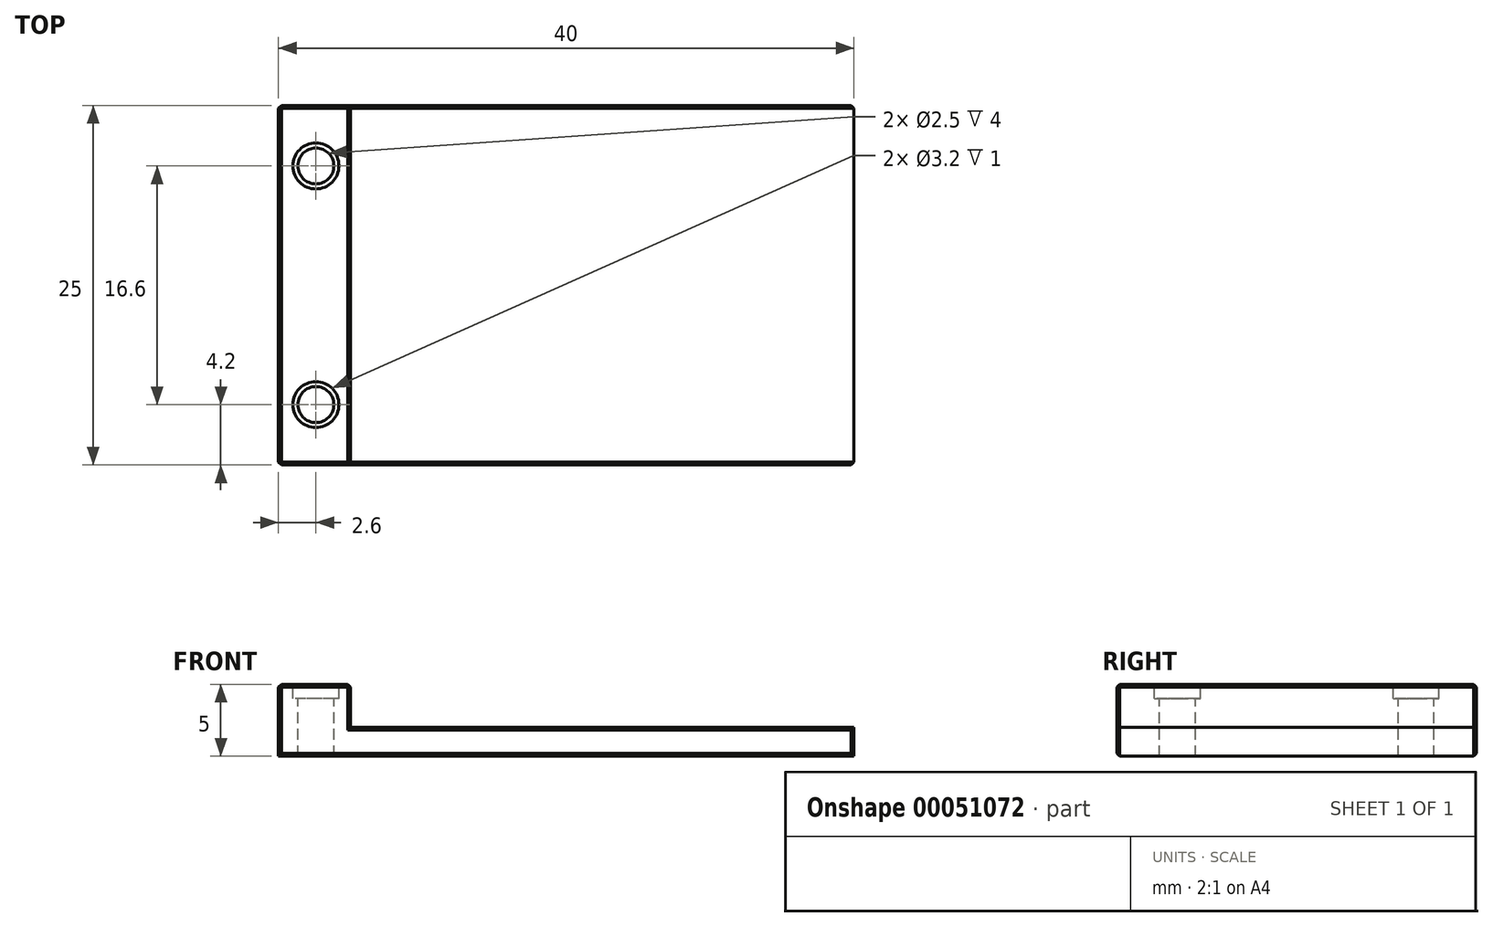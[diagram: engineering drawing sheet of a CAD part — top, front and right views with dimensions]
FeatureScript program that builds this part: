
annotation { "Feature Type Name" : "Feature", "Feature Type Description" : "" }
export const myFeature = defineFeature(function(context is Context, id is Id, definition is map)
    precondition{}
    {
        {
            var Q0;
            Q0=qCreatedBy(makeId("Top.planeOp"),FACE);
            var sketch = newSketch(context, id + "F0", { "sketchPlane" : qUnion([Q0])});
            skLineSegment(sketch, "E0.bottom", {"start": v(0, 0) * mm, "end": v(40, 0) * mm});
            skLineSegment(sketch, "E0.top", {"start": v(0, 25) * mm, "end": v(40, 25) * mm});
            skLineSegment(sketch, "E0.left", {"start": v(0, 0) * mm, "end": v(0, 25) * mm});
            skLineSegment(sketch, "E0.right", {"start": v(40, 0) * mm, "end": v(40, 25) * mm});
            skSolve(sketch);
        }
        {
            var Q0;
            Q0=makeQuery(id+"F0.imprint","IMPRINT",FACE,{"disambiguationData":[TD([[makeQuery(id+"F0.imprint","IMPRINT",EDGE,{"derivedFrom":sQuery(id+"F0.wireOp",EDGE,"E0.bottom")}),1.0]])]});
            extrude(context, id + "F1", {"entities" : qUnion([Q0]), "depth" : 5 * mm});
        }
        {
            var Q0;
            Q0=makeQuery(id+"F1.opExtrude","SWEPT_FACE",FACE,{"disambiguationData":[OSD([sQuery(id+"F0.wireOp",EDGE,"E0.bottom")])]});
            var sketch = newSketch(context, id + "F2", { "sketchPlane" : qUnion([Q0])});
            skLineSegment(sketch, "E1.bottom", {"start": v(5, 5) * mm, "end": v(40, 5) * mm});
            skLineSegment(sketch, "E1.top", {"start": v(5, 2) * mm, "end": v(40, 2) * mm});
            skLineSegment(sketch, "E1.left", {"start": v(5, 5) * mm, "end": v(5, 2) * mm});
            skLineSegment(sketch, "E1.right", {"start": v(40, 5) * mm, "end": v(40, 2) * mm});
            skSolve(sketch);
        }
        {
            var Q0;
            Q0 = qSketchRegion(id + "F2", true);
            extrude(context, id + "F3", {"entities" : qUnion([Q0]), "operationType" : NewBodyOperationType.REMOVE, "oppositeDirection" : true, "depth" : 25 * mm});
        }
        {
            var Q0;
            Q0=makeQuery(id+"F1.opExtrude","CAP_FACE",FACE,{"disambiguationData":[OSD([sQuery(id+"F0.wireOp",EDGE,"E0.bottom"),sQuery(id+"F0.wireOp",EDGE,"E0.top"),sQuery(id+"F0.wireOp",EDGE,"E0.left"),sQuery(id+"F0.wireOp",EDGE,"E0.right")])],"isStart":false});
            var Q1;
            Q1=makeQuery(id+"F1.opExtrude","SWEPT_FACE",FACE,{"disambiguationData":[OSD([sQuery(id+"F0.wireOp",EDGE,"E0.bottom")])]});
            var Q2;
            Q2=makeQuery(id+"F1.opExtrude","SWEPT_FACE",FACE,{"disambiguationData":[OSD([sQuery(id+"F0.wireOp",EDGE,"E0.top")])]});
            chamfer(context, id + "F4", {"entities" : qUnion([Q0, Q1, Q2]), "width" : 0.2 * mm, "tangentPropagation" : true});
        }
        {
            var Q0;
            Q0=makeQuery(id+"F1.opExtrude","CAP_FACE",FACE,{"disambiguationData":[OSD([sQuery(id+"F0.wireOp",EDGE,"E0.bottom"),sQuery(id+"F0.wireOp",EDGE,"E0.top"),sQuery(id+"F0.wireOp",EDGE,"E0.left"),sQuery(id+"F0.wireOp",EDGE,"E0.right")])],"isStart":false});
            var sketch = newSketch(context, id + "F5", { "sketchPlane" : qUnion([Q0])});
            skCircle(sketch, "E2", {"center": v(2.6, 20.8) * mm, "radius": 1.25 * mm});
            skSolve(sketch);
        }
        {
            var Q0;
            Q0=makeQuery(id+"F5.imprint","IMPRINT",FACE,{"disambiguationData":[TD([[makeQuery(id+"F5.imprint","IMPRINT",EDGE,{"derivedFrom":sQuery(id+"F5.wireOp",EDGE,"E2")}),-1.0]])]});
            var sketch = newSketch(context, id + "F6", { "sketchPlane" : qUnion([Q0])});
            skCircle(sketch, "E3", {"center": v(2.6, 4.2) * mm, "radius": 1.25 * mm});
            skSolve(sketch);
        }
        {
            var Q0;
            Q0=sQuery(id+"F5.wireOp",VERTEX,"E2.center");
            var Q1;
            Q1=makeQuery(id+"F1.opExtrude","SWEPT_BODY",BODY,{"disambiguationData":[OSD([sQuery(id+"F0.wireOp",EDGE,"E0.bottom"),sQuery(id+"F0.wireOp",EDGE,"E0.top"),sQuery(id+"F0.wireOp",EDGE,"E0.left"),sQuery(id+"F0.wireOp",EDGE,"E0.right")])]});
            hole(context, id + "F7", {"style" : HoleStyle.C_BORE, "holeDiameter" : 2.5 * mm, "cBoreDiameter" : 3.2 * mm, "cBoreDepth" : 1 * mm, "endStyle" : HoleEndStyle.THROUGH, "locations" : qUnion([Q0]), "scope" : qUnion([Q1])});
        }
        {
            var Q0;
            Q0=sQuery(id+"F6.wireOp",VERTEX,"E3.center");
            var Q1;
            Q1=makeQuery(id+"F1.opExtrude","SWEPT_BODY",BODY,{"disambiguationData":[OSD([sQuery(id+"F0.wireOp",EDGE,"E0.bottom"),sQuery(id+"F0.wireOp",EDGE,"E0.top"),sQuery(id+"F0.wireOp",EDGE,"E0.left"),sQuery(id+"F0.wireOp",EDGE,"E0.right")])]});
            hole(context, id + "F8", {"style" : HoleStyle.C_BORE, "holeDiameter" : 2.5 * mm, "cBoreDiameter" : 3.2 * mm, "cBoreDepth" : 1 * mm, "endStyle" : HoleEndStyle.THROUGH, "locations" : qUnion([Q0]), "scope" : qUnion([Q1])});
        }
    });
